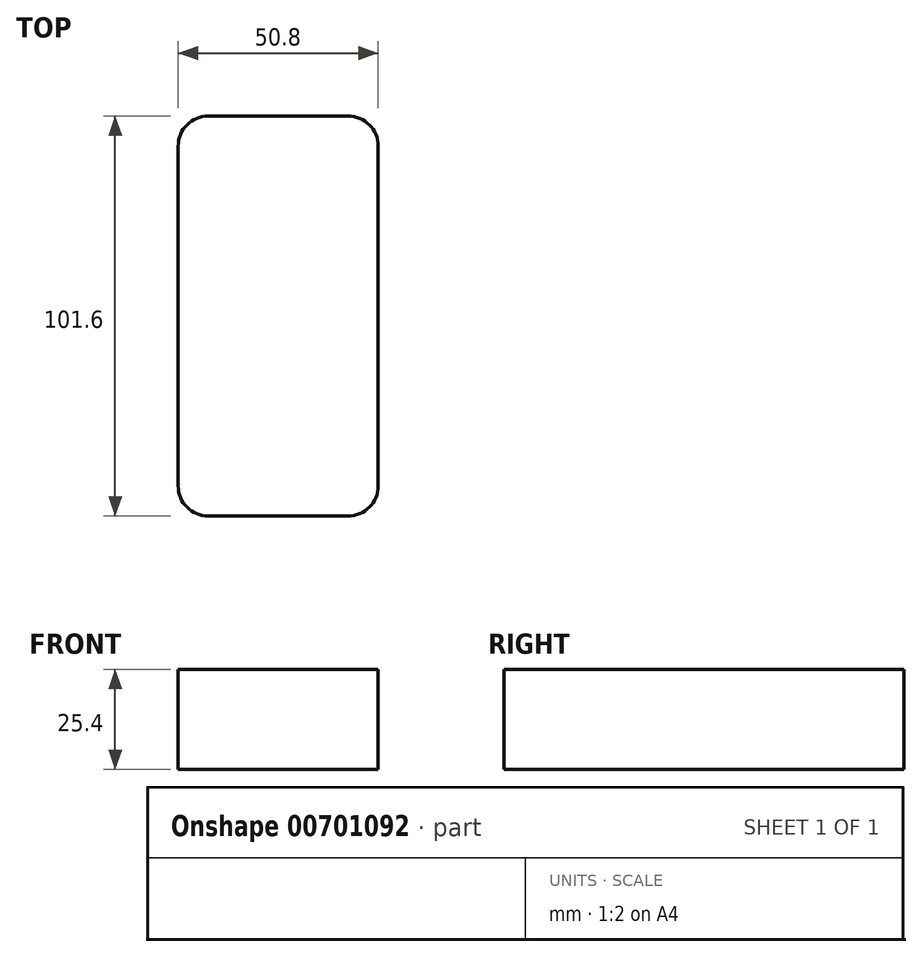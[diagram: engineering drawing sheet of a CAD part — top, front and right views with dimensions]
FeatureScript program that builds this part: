
annotation { "Feature Type Name" : "Feature", "Feature Type Description" : "" }
export const myFeature = defineFeature(function(context is Context, id is Id, definition is map)
    precondition{}
    {
        {
            var Q0;
            Q0=qCreatedBy(makeId("Top.planeOp"),FACE);
            var sketch = newSketch(context, id + "F0", { "sketchPlane" : qUnion([Q0])});
            skLineSegment(sketch, "E0.bottom", {"start": v(0, 0) * mm, "end": v(50.8, 0) * mm});
            skLineSegment(sketch, "E0.top", {"start": v(0, -101.6) * mm, "end": v(50.8, -101.6) * mm});
            skLineSegment(sketch, "E0.left", {"start": v(0, 0) * mm, "end": v(0, -101.6) * mm});
            skLineSegment(sketch, "E0.right", {"start": v(50.8, 0) * mm, "end": v(50.8, -101.6) * mm});
            skSolve(sketch);
        }
        {
            var Q0;
            Q0 = qSketchRegion(id + "F0", true);
            extrude(context, id + "F1", {"entities" : qUnion([Q0]), "depth" : 25.4 * mm, "offsetDistance" : 25.4 * mm});
        }
        {
            var Q0;
            Q0=makeQuery(id+"F1.opExtrude","SWEPT_EDGE",EDGE,{"disambiguationData":[OSD([sQuery(id+"F0.wireOp",EDGE,"E0.bottom"),sQuery(id+"F0.wireOp",EDGE,"E0.left")])]});
            var Q1;
            Q1=makeQuery(id+"F1.opExtrude","SWEPT_EDGE",EDGE,{"disambiguationData":[OSD([sQuery(id+"F0.wireOp",EDGE,"E0.bottom"),sQuery(id+"F0.wireOp",EDGE,"E0.right")])]});
            var Q2;
            Q2=makeQuery(id+"F1.opExtrude","SWEPT_EDGE",EDGE,{"disambiguationData":[OSD([sQuery(id+"F0.wireOp",EDGE,"E0.top"),sQuery(id+"F0.wireOp",EDGE,"E0.left")])]});
            var Q3;
            Q3=makeQuery(id+"F1.opExtrude","SWEPT_EDGE",EDGE,{"disambiguationData":[OSD([sQuery(id+"F0.wireOp",EDGE,"E0.top"),sQuery(id+"F0.wireOp",EDGE,"E0.right")])]});
            fillet(context, id + "F2", {"entities" : qUnion([Q0, Q1, Q2, Q3]), "radius" : 7.62 * mm, "tangentPropagation" : true, "allowEdgeOverflow" : false});
        }
    });
